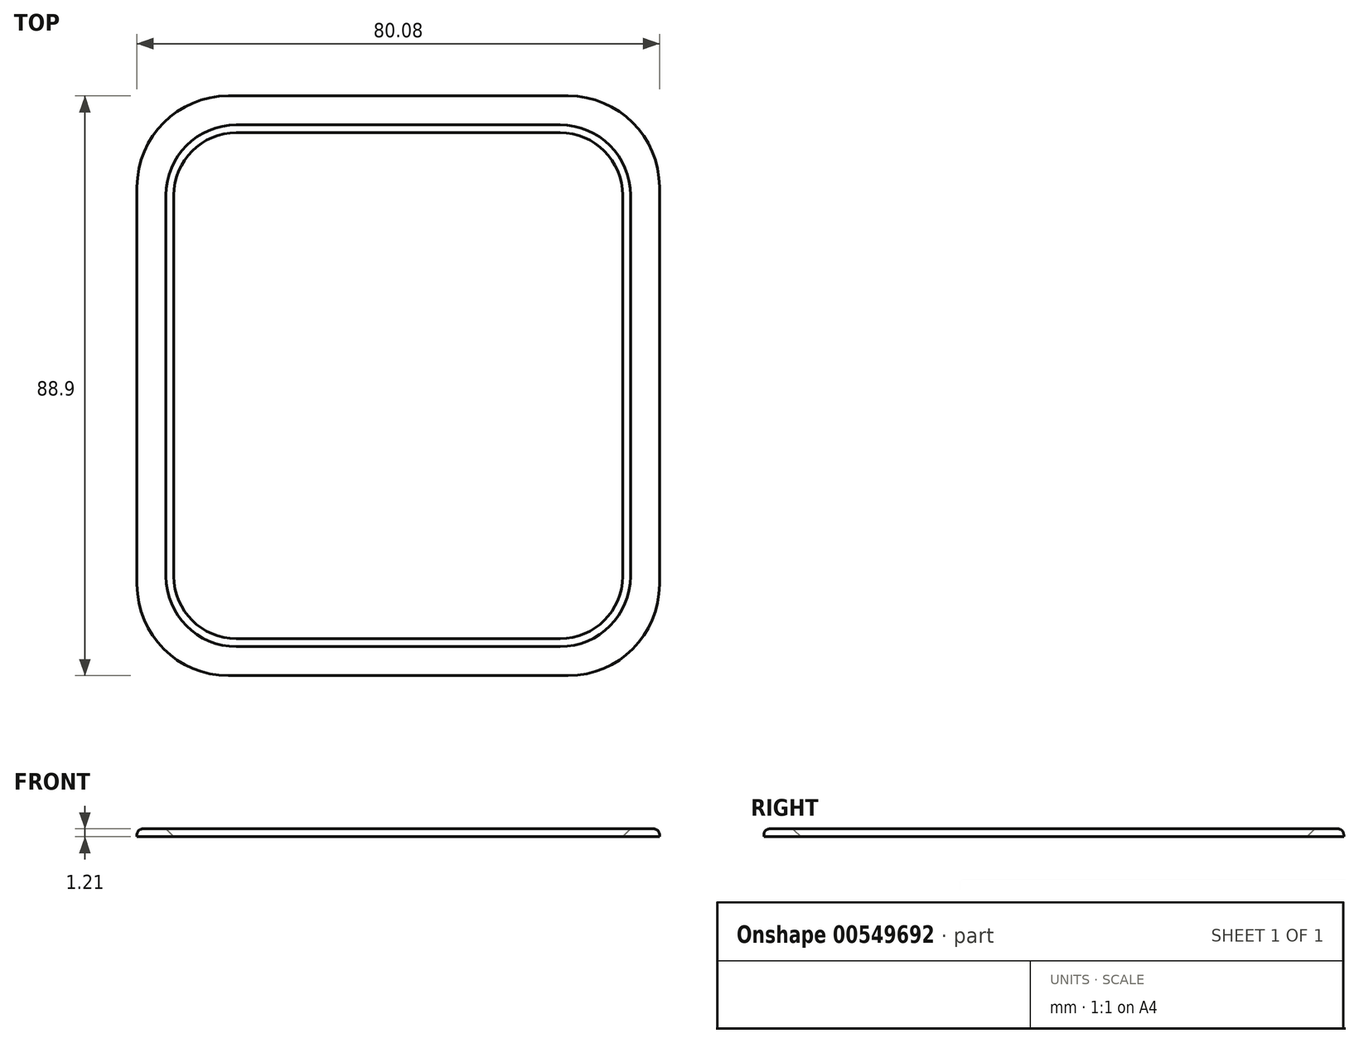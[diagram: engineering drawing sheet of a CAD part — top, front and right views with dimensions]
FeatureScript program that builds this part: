
annotation { "Feature Type Name" : "Feature", "Feature Type Description" : "" }
export const myFeature = defineFeature(function(context is Context, id is Id, definition is map)
    precondition{}
    {
        {
            var Q0;
            Q0=qCreatedBy(makeId("Top.planeOp"),FACE);
            var sketch = newSketch(context, id + "F0", { "sketchPlane" : qUnion([Q0])});
            skLineSegment(sketch, "E0.bottom", {"start": v(26.06, 44.45) * mm, "end": v(-26.06, 44.45) * mm});
            skLineSegment(sketch, "E0.top", {"start": v(26.06, -44.45) * mm, "end": v(-26.06, -44.45) * mm});
            skLineSegment(sketch, "E0.left", {"start": v(40.04, 30.47) * mm, "end": v(40.04, -30.47) * mm});
            skLineSegment(sketch, "E0.right", {"start": v(-40.04, 30.47) * mm, "end": v(-40.04, -30.47) * mm});
            skPoint(sketch, "E0.middle", {"position": v(0, 0) * mm});
            skPoint(sketch, "E1.visualSharp", {"position": v(-40.04, 44.45) * mm});
            skArc(sketch, "E1.filletArc", {"start": v(-26.06, 44.45) * mm, "mid": v(-35.95, 40.35) * mm, "end": v(-40.04, 30.47) * mm});
            skPoint(sketch, "E2.visualSharp", {"position": v(40.04, 44.45) * mm});
            skArc(sketch, "E2.filletArc", {"start": v(40.04, 30.47) * mm, "mid": v(35.95, 40.35) * mm, "end": v(26.06, 44.45) * mm});
            skPoint(sketch, "E3.visualSharp", {"position": v(40.04, -44.45) * mm});
            skArc(sketch, "E3.filletArc", {"start": v(26.06, -44.45) * mm, "mid": v(35.95, -40.35) * mm, "end": v(40.04, -30.47) * mm});
            skPoint(sketch, "E4.visualSharp", {"position": v(-40.04, -44.45) * mm});
            skArc(sketch, "E4.filletArc", {"start": v(-40.04, -30.47) * mm, "mid": v(-35.95, -40.35) * mm, "end": v(-26.06, -44.45) * mm});
            skSolve(sketch);
        }
        {
            var Q0;
            Q0=qCreatedBy(makeId("Top.planeOp"),FACE);
            var sketch = newSketch(context, id + "F1", { "sketchPlane" : qUnion([Q0])});
            skLineSegment(sketch, "E5.bottom", {"start": v(24.8, 38.74) * mm, "end": v(-24.8, 38.74) * mm});
            skLineSegment(sketch, "E5.top", {"start": v(24.8, -38.74) * mm, "end": v(-24.8, -38.74) * mm});
            skLineSegment(sketch, "E5.left", {"start": v(34.33, 29.21) * mm, "end": v(34.33, -29.21) * mm});
            skLineSegment(sketch, "E5.right", {"start": v(-34.33, 29.21) * mm, "end": v(-34.33, -29.21) * mm});
            skPoint(sketch, "E5.middle", {"position": v(0, 0) * mm});
            skPoint(sketch, "E6.visualSharp", {"position": v(-34.33, 38.74) * mm});
            skArc(sketch, "E6.filletArc", {"start": v(-24.8, 38.74) * mm, "mid": v(-31.54, 35.95) * mm, "end": v(-34.33, 29.21) * mm});
            skPoint(sketch, "E7.visualSharp", {"position": v(34.33, 38.74) * mm});
            skArc(sketch, "E7.filletArc", {"start": v(34.33, 29.21) * mm, "mid": v(31.54, 35.95) * mm, "end": v(24.8, 38.74) * mm});
            skPoint(sketch, "E8.visualSharp", {"position": v(34.33, -38.74) * mm});
            skArc(sketch, "E8.filletArc", {"start": v(24.8, -38.74) * mm, "mid": v(31.54, -35.95) * mm, "end": v(34.33, -29.21) * mm});
            skPoint(sketch, "E9.visualSharp", {"position": v(-34.33, -38.74) * mm});
            skArc(sketch, "E9.filletArc", {"start": v(-34.33, -29.21) * mm, "mid": v(-31.54, -35.95) * mm, "end": v(-24.8, -38.74) * mm});
            skSolve(sketch);
        }
        {
            var Q0;
            Q0=makeQuery(id+"F0.imprint","IMPRINT",FACE,{"disambiguationData":[TD([[makeQuery(id+"F0.imprint","IMPRINT",EDGE,{"derivedFrom":sQuery(id+"F0.wireOp",EDGE,"E0.bottom")}),1.0]])]});
            extrude(context, id + "F2", {"entities" : qUnion([Q0]), "depth" : 1.2 * mm, "offsetDistance" : 25.4 * mm});
        }
        {
            var Q0;
            Q0 = qSketchRegion(id + "F1", true);
            var Q1;
            Q1=makeQuery(id+"F2.opExtrude","CAP_FACE",FACE,{"disambiguationData":[OSD([sQuery(id+"F0.wireOp",EDGE,"E0.bottom"),sQuery(id+"F0.wireOp",EDGE,"E0.top"),sQuery(id+"F0.wireOp",EDGE,"E0.left"),sQuery(id+"F0.wireOp",EDGE,"E0.right"),sQuery(id+"F0.wireOp",EDGE,"E1.filletArc"),sQuery(id+"F0.wireOp",EDGE,"E2.filletArc"),sQuery(id+"F0.wireOp",EDGE,"E3.filletArc"),sQuery(id+"F0.wireOp",EDGE,"E4.filletArc")])],"isStart":false});
            extrude(context, id + "F3", {"entities" : qUnion([Q0, Q1]), "operationType" : NewBodyOperationType.REMOVE, "endBound" : BoundingType.THROUGH_ALL, "depth" : 25.4 * mm, "offsetDistance" : 25.4 * mm});
        }
        {
            var Q0;
            Q0=makeQuery(id+"F2.opExtrude","CAP_EDGE",EDGE,{"disambiguationData":[OSD([sQuery(id+"F0.wireOp",EDGE,"E0.right")])],"isStart":false});
            fillet(context, id + "F4", {"entities" : qUnion([Q0]), "radius" : 0.88 * mm, "tangentPropagation" : true, "allowEdgeOverflow" : false});
        }
        {
            var Q0;
            {var subQ0=sQuery(id+"F0.wireOp",EDGE,"E4.filletArc");var subQ1=sQuery(id+"F0.wireOp",EDGE,"E3.filletArc");var subQ2=sQuery(id+"F0.wireOp",EDGE,"E2.filletArc");var subQ3=sQuery(id+"F0.wireOp",EDGE,"E1.filletArc");var subQ4=sQuery(id+"F0.wireOp",EDGE,"E0.right");var subQ5=sQuery(id+"F0.wireOp",EDGE,"E0.left");var subQ6=sQuery(id+"F0.wireOp",EDGE,"E0.top");var subQ7=sQuery(id+"F0.wireOp",EDGE,"E0.bottom");Q0=makeQuery(id+"F3.boolean.opBoolean","INTERSECT",EDGE,{"derivedFrom":[makeQuery(id+"F2.opExtrude","CAP_FACE",FACE,{"disambiguationData":[OSD([subQ7,subQ6,subQ5,subQ4,subQ3,subQ2,subQ1,subQ0])],"isStart":false}),makeQuery(id+"F3.opExtrude","SWEPT_FACE",FACE,{"disambiguationData":[OSD([sQuery(id+"F1.wireOp",EDGE,"E5.right")])]}),makeQuery(id+"F3.opExtrude","CAP_FACE",FACE,{"disambiguationData":[OSD([subQ7,subQ6,subQ5,subQ4,subQ3,subQ2,subQ1,subQ0])],"isStart":true})]});}
            chamfer(context, id + "F5", {"entities" : qUnion([Q0]), "width" : 1.27 * mm, "tangentPropagation" : true});
        }
    });
